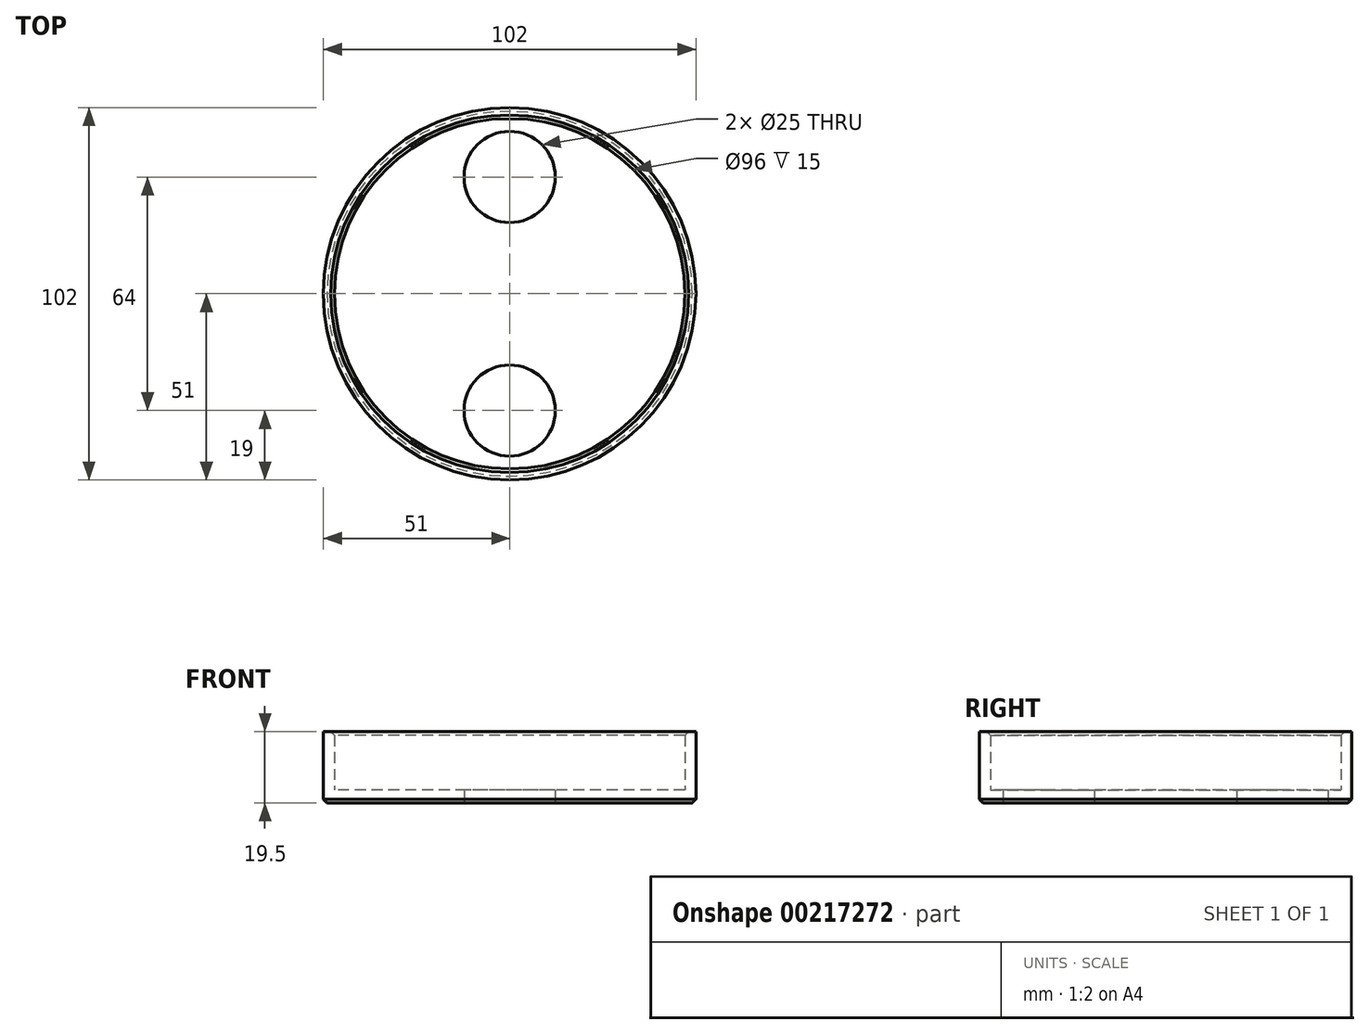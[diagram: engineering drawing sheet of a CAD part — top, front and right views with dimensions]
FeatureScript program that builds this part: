
annotation { "Feature Type Name" : "Feature", "Feature Type Description" : "" }
export const myFeature = defineFeature(function(context is Context, id is Id, definition is map)
    precondition{}
    {
        {
            var Q0;
            Q0=qCreatedBy(makeId("Top.planeOp"),FACE);
            var sketch = newSketch(context, id + "F0", { "sketchPlane" : qUnion([Q0])});
            skCircle(sketch, "E0", {"center": v(0, 0) * mm, "radius": 51 * mm});
            skSolve(sketch);
        }
        {
            var Q0;
            Q0 = qSketchRegion(id + "F0", true);
            extrude(context, id + "F1", {"entities" : qUnion([Q0]), "depth" : 3.5 * mm});
        }
        {
            var Q0;
            Q0=makeQuery(id+"F1.opExtrude","CAP_FACE",FACE,{"disambiguationData":[OSD([sQuery(id+"F0.wireOp",EDGE,"E0")])],"isStart":false});
            var sketch = newSketch(context, id + "F2", { "sketchPlane" : qUnion([Q0])});
            skCircle(sketch, "E1", {"center": v(0, 0) * mm, "radius": 51 * mm});
            skCircle(sketch, "E2", {"center": v(0, 0) * mm, "radius": 48 * mm});
            skSolve(sketch);
        }
        {
            var Q0;
            Q0 = qSketchRegion(id + "F2", true);
            extrude(context, id + "F3", {"entities" : qUnion([Q0]), "operationType" : NewBodyOperationType.ADD, "depth" : 16 * mm});
        }
        {
            var Q0;
            Q0=makeQuery(id+"F1.opExtrude","CAP_FACE",FACE,{"disambiguationData":[OSD([sQuery(id+"F0.wireOp",EDGE,"E0")])],"isStart":true});
            var sketch = newSketch(context, id + "F4", { "sketchPlane" : qUnion([Q0])});
            skCircle(sketch, "E3", {"center": v(0, 32) * mm, "radius": 12.5 * mm});
            skCircle(sketch, "E4.MirrorC", {"center": v(0, -32) * mm, "radius": 12.5 * mm});
            skSolve(sketch);
        }
        {
            var Q0;
            Q0 = qSketchRegion(id + "F4", true);
            extrude(context, id + "F5", {"entities" : qUnion([Q0]), "operationType" : NewBodyOperationType.REMOVE, "oppositeDirection" : true, "depth" : 25 * mm});
        }
        {
            var Q0;
            Q0=makeQuery(id+"F1.opExtrude","CAP_EDGE",EDGE,{"disambiguationData":[OSD([sQuery(id+"F0.wireOp",EDGE,"E0")])],"isStart":true});
            var Q1;
            Q1=makeQuery(id+"F5.boolean.opBoolean","COPY",EDGE,{"derivedFrom":makeQuery(id+"F5.opExtrude","CAP_EDGE",EDGE,{"disambiguationData":[OSD([sQuery(id+"F4.wireOp",EDGE,"E4.MirrorC")])],"isStart":true})});
            var Q2;
            Q2=makeQuery(id+"F5.boolean.opBoolean","COPY",EDGE,{"derivedFrom":makeQuery(id+"F5.opExtrude","CAP_EDGE",EDGE,{"disambiguationData":[OSD([sQuery(id+"F4.wireOp",EDGE,"E3")])],"isStart":true})});
            chamfer(context, id + "F6", {"entities" : qUnion([Q0, Q1, Q2]), "width" : 1 * mm, "tangentPropagation" : true});
        }
        {
            var Q0;
            Q0=makeQuery(id+"F3.opExtrude","CAP_EDGE",EDGE,{"disambiguationData":[OSD([sQuery(id+"F2.wireOp",EDGE,"E2")])],"isStart":false});
            chamfer(context, id + "F7", {"entities" : qUnion([Q0]), "width" : 1 * mm, "tangentPropagation" : true});
        }
    });
